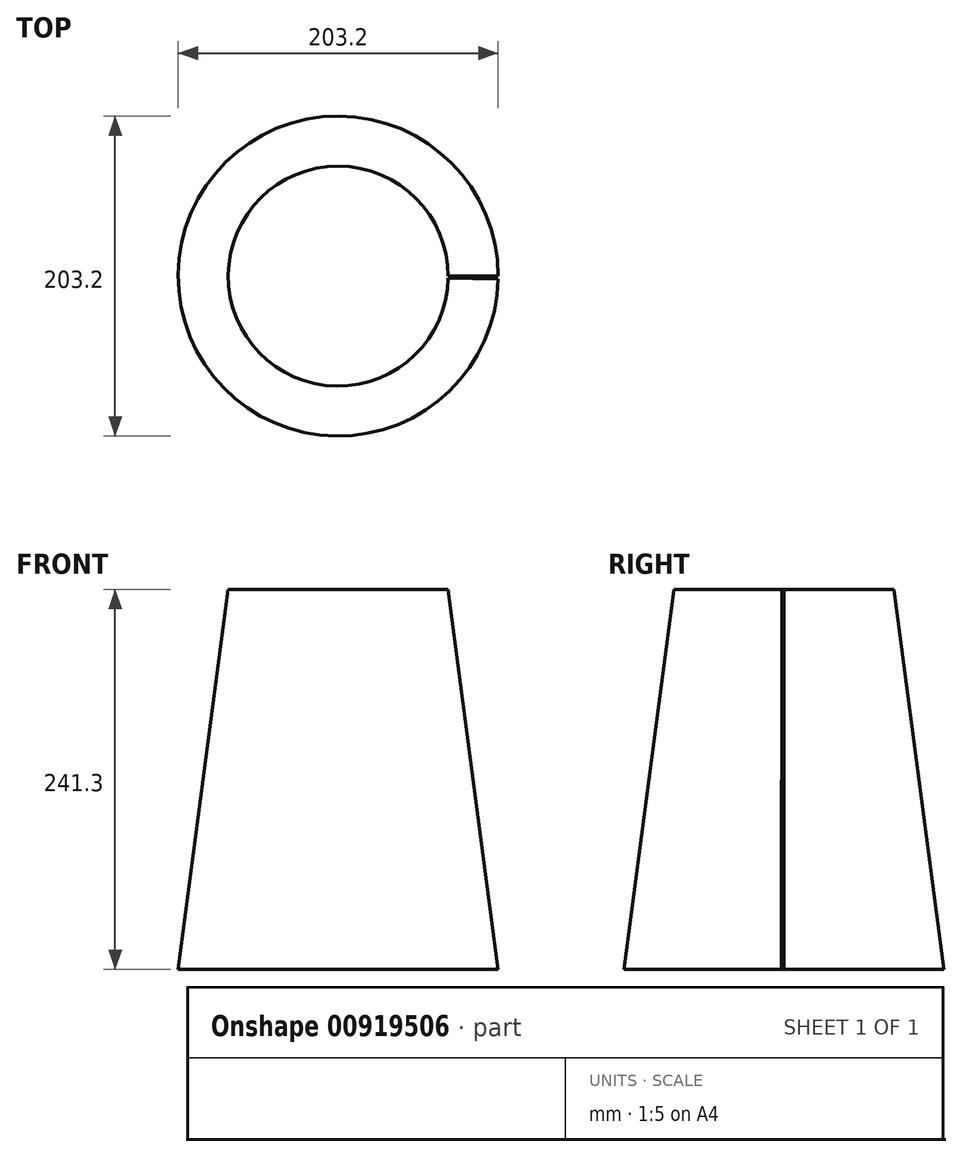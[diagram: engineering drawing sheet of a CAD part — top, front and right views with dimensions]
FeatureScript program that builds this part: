
annotation { "Feature Type Name" : "Feature", "Feature Type Description" : "" }
export const myFeature = defineFeature(function(context is Context, id is Id, definition is map)
    precondition{}
    {
        {
            var Q0;
            Q0=qCreatedBy(makeId("Front.planeOp"),FACE);
            var sketch = newSketch(context, id + "F0", { "sketchPlane" : qUnion([Q0])});
            skLineSegment(sketch, "E0", {"start": v(0, 241.3) * mm, "end": v(69.85, 241.3) * mm, "construction": true});
            skLineSegment(sketch, "E1", {"start": v(0, 0) * mm, "end": v(101.6, 0) * mm, "construction": true});
            skLineSegment(sketch, "E2", {"start": v(101.6, 0) * mm, "end": v(69.85, 241.3) * mm});
            skLineSegment(sketch, "E3", {"start": v(0, -177.14) * mm, "end": v(0, 308.59) * mm, "construction": true});
            skSolve(sketch);
        }
        {
            var Q0;
            Q0=sQuery(id+"F0.wireOp",EDGE,"E2");
            var Q1;
            Q1=sQuery(id+"F0.wireOp",EDGE,"E3");
            revolve(context, id + "F1", {"bodyType" : ToolBodyType.SURFACE, "surfaceOperationType" : NewSurfaceOperationType.NEW, "surfaceEntities" : qUnion([Q0]), "axis" : qUnion([Q1]), "revolveType" : RevolveType.ONE_DIRECTION, "angle" : 359 * degree});
        }
    });
